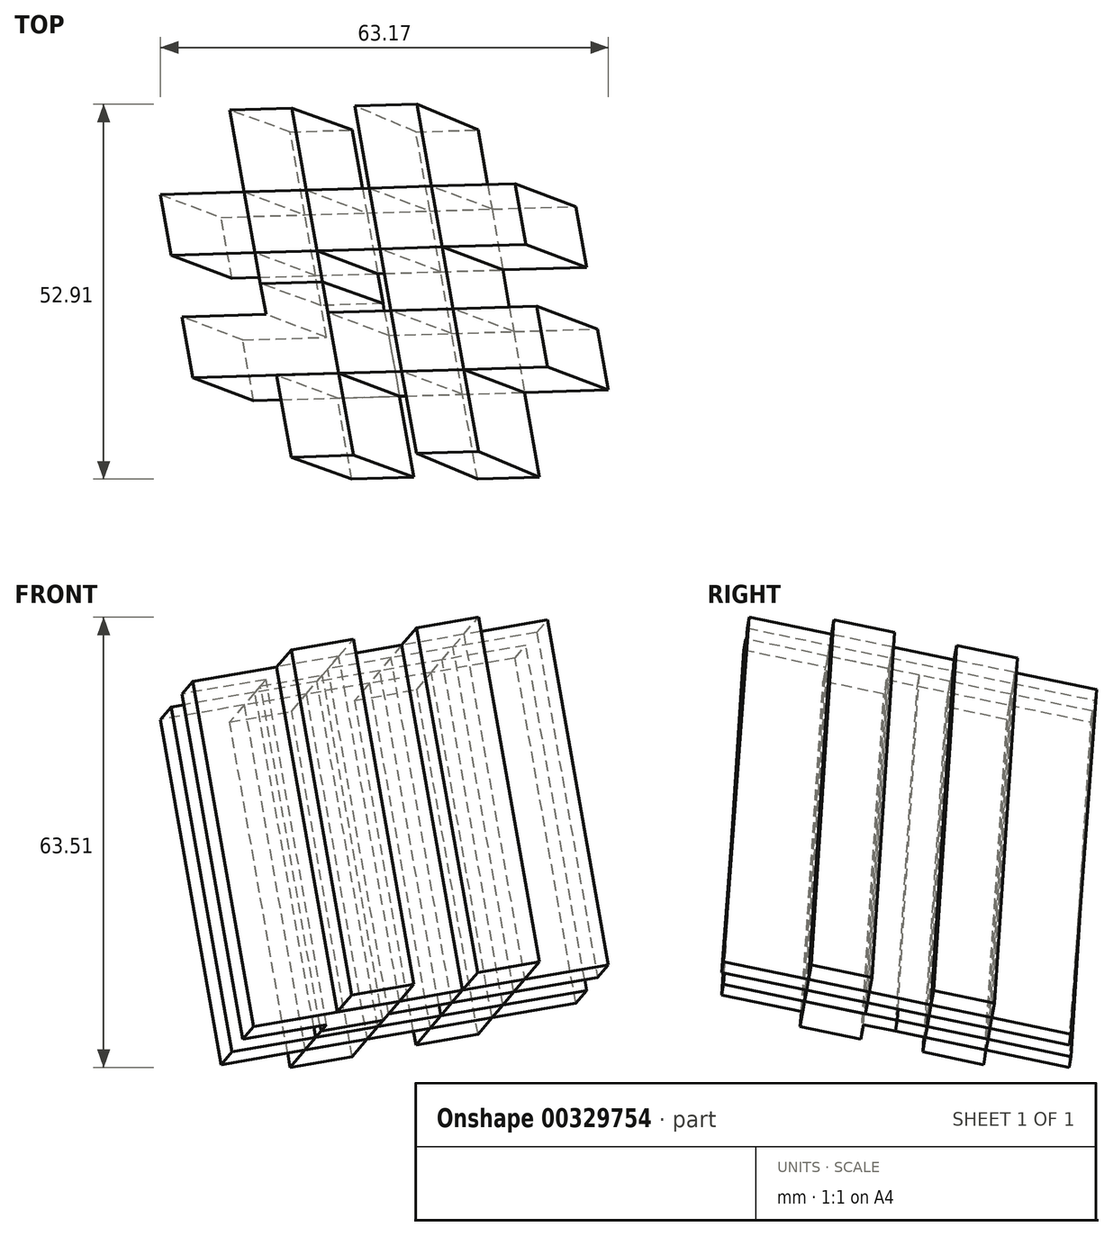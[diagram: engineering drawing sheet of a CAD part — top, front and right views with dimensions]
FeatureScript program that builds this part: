
annotation { "Feature Type Name" : "Feature", "Feature Type Description" : "" }
export const myFeature = defineFeature(function(context is Context, id is Id, definition is map)
    precondition{}
    {
        {
            var Q0;
            Q0=qCreatedBy(makeId("Front.planeOp"),FACE);
            var sketch = newSketch(context, id + "F0", { "sketchPlane" : qUnion([Q0])});
            skLineSegment(sketch, "E0", {"start": v(74.16, 50.8) * mm, "end": v(-71.4, 50.8) * mm});
            skSolve(sketch);
        }
        {
            var Q0;
            Q0=qCreatedBy(makeId("Top.planeOp"),FACE);
            var sketch = newSketch(context, id + "F1", { "sketchPlane" : qUnion([Q0])});
            skLineSegment(sketch, "E1", {"start": v(-74.62, 0) * mm, "end": v(72.22, 0) * mm});
            skSolve(sketch);
        }
        {
            var Q0;
            Q0=qCreatedBy(makeId("Top.planeOp"),FACE);
            var Q1;
            Q1=sQuery(id+"F1.wireOp",EDGE,"E1");
            cPlane(context, id + "F2", {"entities" : qUnion([Q0, Q1]), "cplaneType" : CPlaneType.LINE_ANGLE, "offset" : 0 * mm, "angle" : 170 * degree, "width" : 152.4 * mm, "height" : 152.4 * mm});
        }
        {
            var Q0;
            Q0=qCreatedBy(id+"F2.planeOp",FACE);
            var sketch = newSketch(context, id + "F3", { "sketchPlane" : qUnion([Q0])});
            skLineSegment(sketch, "E2", {"start": v(0, 68.21) * mm, "end": v(0, -63.3) * mm});
            skSolve(sketch);
        }
        {
            var Q0;
            Q0=sQuery(id+"F3.wireOp",EDGE,"E2");
            var Q1;
            Q1=qCreatedBy(id+"F2.planeOp",FACE);
            cPlane(context, id + "F4", {"entities" : qUnion([Q0, Q1]), "cplaneType" : CPlaneType.LINE_ANGLE, "offset" : 25.4 * mm, "angle" : 10 * degree, "width" : 152.4 * mm, "height" : 152.4 * mm});
        }
        {
            var Q0;
            Q0=qCreatedBy(id+"F4.planeOp",FACE);
            var sketch = newSketch(context, id + "F5", { "sketchPlane" : qUnion([Q0])});
            skLineSegment(sketch, "E3.bottom", {"start": v(-23.07, 13.2) * mm, "end": v(27.73, 13.2) * mm});
            skLineSegment(sketch, "E3.top", {"start": v(-24.62, 4.44) * mm, "end": v(26.18, 4.45) * mm});
            skLineSegment(sketch, "E3.left", {"start": v(-23.07, 13.2) * mm, "end": v(-24.62, 4.45) * mm});
            skLineSegment(sketch, "E3.right", {"start": v(27.73, 13.2) * mm, "end": v(26.18, 4.45) * mm});
            skLineSegment(sketch, "E4.bottom", {"start": v(-26.18, -4.45) * mm, "end": v(24.62, -4.44) * mm});
            skLineSegment(sketch, "E4.top", {"start": v(-27.73, -13.2) * mm, "end": v(23.07, -13.2) * mm});
            skLineSegment(sketch, "E4.left", {"start": v(-26.18, -4.45) * mm, "end": v(-27.73, -13.2) * mm});
            skLineSegment(sketch, "E4.right", {"start": v(24.62, -4.44) * mm, "end": v(23.07, -13.2) * mm});
            skLineSegment(sketch, "E5", {"start": v(-9.02, 24.88) * mm, "end": v(-17.84, -25.15) * mm});
            skLineSegment(sketch, "E6", {"start": v(-17.84, -25.15) * mm, "end": v(-8.95, -25.15) * mm});
            skLineSegment(sketch, "E7", {"start": v(-8.95, -25.15) * mm, "end": v(-0.13, 24.88) * mm});
            skLineSegment(sketch, "E8", {"start": v(-0.13, 24.88) * mm, "end": v(-9.02, 24.88) * mm});
            skLineSegment(sketch, "E9", {"start": v(0.78, 4.45) * mm, "end": v(-0.78, -4.45) * mm});
            skPoint(sketch, "E10", {"position": v(0, 0) * mm});
            skPoint(sketch, "E11", {"position": v(-4.54, -0.14) * mm});
            skLineSegment(sketch, "E12", {"start": v(9, 25.43) * mm, "end": v(0.18, -24.6) * mm});
            skLineSegment(sketch, "E13", {"start": v(0.18, -24.6) * mm, "end": v(9.07, -24.6) * mm});
            skLineSegment(sketch, "E14", {"start": v(9.07, -24.6) * mm, "end": v(17.89, 25.43) * mm});
            skLineSegment(sketch, "E15", {"start": v(17.89, 25.43) * mm, "end": v(9, 25.43) * mm});
            skPoint(sketch, "E16", {"position": v(13.48, 0.41) * mm});
            skPoint(sketch, "E17", {"position": v(4.54, 0.14) * mm});
            skLineSegment(sketch, "E18", {"start": v(4.54, 0.14) * mm, "end": v(0, 0) * mm});
            skLineSegment(sketch, "E19", {"start": v(-4.54, -0.14) * mm, "end": v(0, 0) * mm});
            skLineSegment(sketch, "E20", {"start": v(0.78, 4.45) * mm, "end": v(0, 0) * mm});
            skLineSegment(sketch, "E21", {"start": v(-4.54, -0.14) * mm, "end": v(-13.43, -0.14) * mm});
            skPoint(sketch, "E22", {"position": v(2.19, -13.2) * mm});
            skPoint(sketch, "E23", {"position": v(-14.19, -4.45) * mm});
            skSolve(sketch);
        }
        {
            var Q0;
            Q0=qCreatedBy(makeId("Top.planeOp"),FACE);
            var Q1;
            Q1=sQuery(id+"F0.wireOp",EDGE,"E0");
            cPlane(context, id + "F6", {"entities" : qUnion([Q0, Q1]), "cplaneType" : CPlaneType.LINE_ANGLE, "offset" : 50.8 * mm, "angle" : 10 * degree, "width" : 152.4 * mm, "height" : 152.4 * mm});
        }
        {
            var Q0;
            Q0=qCreatedBy(id+"F6.planeOp",FACE);
            var sketch = newSketch(context, id + "F7", { "sketchPlane" : qUnion([Q0])});
            skLineSegment(sketch, "E24", {"start": v(0, -55.77) * mm, "end": v(0, 79.16) * mm});
            skSolve(sketch);
        }
        {
            var Q0;
            Q0=sQuery(id+"F7.wireOp",EDGE,"E24");
            var Q1;
            Q1=qCreatedBy(id+"F6.planeOp",FACE);
            cPlane(context, id + "F8", {"entities" : qUnion([Q0, Q1]), "cplaneType" : CPlaneType.LINE_ANGLE, "offset" : 25.4 * mm, "angle" : 10 * degree, "width" : 152.4 * mm, "height" : 152.4 * mm});
        }
        {
            var Q0;
            Q0=qCreatedBy(id+"F8.planeOp",FACE);
            var sketch = newSketch(context, id + "F9", { "sketchPlane" : qUnion([Q0])});
            skLineSegment(sketch, "E25.bottom", {"start": v(-130.18, 7.92) * mm, "end": v(-79.38, 7.92) * mm});
            skLineSegment(sketch, "E25.top", {"start": v(-131.73, -0.83) * mm, "end": v(-80.93, -0.83) * mm});
            skLineSegment(sketch, "E25.left", {"start": v(-130.18, 7.92) * mm, "end": v(-131.73, -0.83) * mm});
            skLineSegment(sketch, "E25.right", {"start": v(-79.38, 7.92) * mm, "end": v(-80.93, -0.83) * mm});
            skLineSegment(sketch, "E26.bottom", {"start": v(-133.3, -9.72) * mm, "end": v(-82.5, -9.72) * mm});
            skLineSegment(sketch, "E26.top", {"start": v(-134.84, -18.48) * mm, "end": v(-84.04, -18.48) * mm});
            skLineSegment(sketch, "E26.left", {"start": v(-133.3, -9.72) * mm, "end": v(-134.84, -18.48) * mm});
            skLineSegment(sketch, "E26.right", {"start": v(-82.5, -9.72) * mm, "end": v(-84.04, -18.48) * mm});
            skLineSegment(sketch, "E27", {"start": v(-116.1, 19.74) * mm, "end": v(-124.92, -30.29) * mm});
            skLineSegment(sketch, "E28", {"start": v(-124.92, -30.29) * mm, "end": v(-116.03, -30.29) * mm});
            skLineSegment(sketch, "E29", {"start": v(-116.03, -30.29) * mm, "end": v(-107.21, 19.74) * mm});
            skLineSegment(sketch, "E30", {"start": v(-107.21, 19.74) * mm, "end": v(-116.1, 19.74) * mm});
            skLineSegment(sketch, "E31", {"start": v(-106.33, -0.83) * mm, "end": v(-107.9, -9.72) * mm});
            skPoint(sketch, "E32", {"position": v(-107.1, -5.28) * mm});
            skPoint(sketch, "E33", {"position": v(-111.62, -5.28) * mm});
            skLineSegment(sketch, "E34", {"start": v(-98.19, 19.74) * mm, "end": v(-107, -30.29) * mm});
            skLineSegment(sketch, "E35", {"start": v(-107, -30.29) * mm, "end": v(-98.12, -30.29) * mm});
            skLineSegment(sketch, "E36", {"start": v(-98.12, -30.29) * mm, "end": v(-89.3, 19.74) * mm});
            skLineSegment(sketch, "E37", {"start": v(-89.3, 19.74) * mm, "end": v(-98.19, 19.74) * mm});
            skLineSegment(sketch, "E38", {"start": v(-111.62, -5.28) * mm, "end": v(-107.1, -5.28) * mm});
            skLineSegment(sketch, "E39", {"start": v(-106.33, -0.83) * mm, "end": v(-107.1, -5.28) * mm});
            skPoint(sketch, "E40", {"position": v(-102.6, -5.28) * mm});
            skLineSegment(sketch, "E41", {"start": v(-107.1, -5.28) * mm, "end": v(-102.6, -5.28) * mm});
            skLineSegment(sketch, "E42.MirrorCS", {"start": v(124.48, -5.28) * mm, "end": v(119.97, -5.28) * mm});
            skLineSegment(sketch, "E43.MirrorCS", {"start": v(123.7, -0.83) * mm, "end": v(124.48, -5.28) * mm});
            skLineSegment(sketch, "E44.MirrorCS", {"start": v(129, -5.28) * mm, "end": v(124.48, -5.28) * mm});
            skLineSegment(sketch, "E45.MirrorCS", {"start": v(123.7, -0.83) * mm, "end": v(125.27, -9.72) * mm});
            skLineSegment(sketch, "E46.MirrorCS", {"start": v(115.5, -30.29) * mm, "end": v(106.67, 19.74) * mm});
            skLineSegment(sketch, "E47.MirrorCS", {"start": v(147.56, 7.92) * mm, "end": v(96.76, 7.92) * mm});
            skLineSegment(sketch, "E48.MirrorCS", {"start": v(152.21, -18.48) * mm, "end": v(101.41, -18.48) * mm});
            skPoint(sketch, "E49.MirrorP", {"position": v(124.48, -5.28) * mm});
            skPoint(sketch, "E50.MirrorP", {"position": v(129, -5.28) * mm});
            skPoint(sketch, "E51.MirrorP", {"position": v(119.97, -5.28) * mm});
            skLineSegment(sketch, "E52.MirrorCS", {"start": v(124.59, 19.74) * mm, "end": v(133.48, 19.74) * mm});
            skLineSegment(sketch, "E53.MirrorCS", {"start": v(150.67, -9.72) * mm, "end": v(152.21, -18.48) * mm});
            skLineSegment(sketch, "E54.MirrorCS", {"start": v(149.1, -0.83) * mm, "end": v(98.3, -0.83) * mm});
            skLineSegment(sketch, "E55.MirrorCS", {"start": v(142.3, -30.29) * mm, "end": v(133.4, -30.29) * mm});
            skLineSegment(sketch, "E56.MirrorCS", {"start": v(124.38, -30.29) * mm, "end": v(115.5, -30.29) * mm});
            skLineSegment(sketch, "E57.MirrorCS", {"start": v(133.48, 19.74) * mm, "end": v(142.3, -30.29) * mm});
            skLineSegment(sketch, "E58.MirrorCS", {"start": v(147.56, 7.92) * mm, "end": v(149.1, -0.83) * mm});
            skLineSegment(sketch, "E59.MirrorCS", {"start": v(115.56, 19.74) * mm, "end": v(124.38, -30.29) * mm});
            skLineSegment(sketch, "E60.MirrorCS", {"start": v(150.67, -9.72) * mm, "end": v(99.87, -9.72) * mm});
            skLineSegment(sketch, "E61.MirrorCS", {"start": v(96.76, 7.92) * mm, "end": v(98.3, -0.83) * mm});
            skLineSegment(sketch, "E62.MirrorCS", {"start": v(133.4, -30.29) * mm, "end": v(124.59, 19.74) * mm});
            skLineSegment(sketch, "E63.MirrorCS", {"start": v(99.87, -9.72) * mm, "end": v(101.41, -18.48) * mm});
            skLineSegment(sketch, "E64.MirrorCS", {"start": v(106.67, 19.74) * mm, "end": v(115.56, 19.74) * mm});
            skLineSegment(sketch, "E65", {"start": v(-107.1, -5.28) * mm, "end": v(0, -5.28) * mm});
            skPoint(sketch, "E66", {"position": v(-53.55, -5.28) * mm});
            skPoint(sketch, "E67", {"position": v(-53.55, -7.97) * mm});
            skLineSegment(sketch, "E68", {"start": v(-53.55, -7.97) * mm, "end": v(-53.55, -5.28) * mm});
            skLineSegment(sketch, "E69.MirrorCS", {"start": v(0, -5.28) * mm, "end": v(-4.51, -5.28) * mm});
            skLineSegment(sketch, "E70.MirrorCS", {"start": v(-0.78, -0.83) * mm, "end": v(0, -5.28) * mm});
            skLineSegment(sketch, "E71.MirrorCS", {"start": v(-0.1, -30.29) * mm, "end": v(-9, -30.29) * mm});
            skLineSegment(sketch, "E72.MirrorCS", {"start": v(0.1, 19.74) * mm, "end": v(9, 19.74) * mm});
            skLineSegment(sketch, "E73.MirrorCS", {"start": v(23.07, 7.92) * mm, "end": v(24.62, -0.83) * mm});
            skLineSegment(sketch, "E74.MirrorCS", {"start": v(17.81, -30.29) * mm, "end": v(8.92, -30.29) * mm});
            skLineSegment(sketch, "E75.MirrorCS", {"start": v(26.18, -9.72) * mm, "end": v(27.73, -18.48) * mm});
            skLineSegment(sketch, "E76.MirrorCS", {"start": v(-24.62, -9.72) * mm, "end": v(-23.07, -18.48) * mm});
            skLineSegment(sketch, "E77.MirrorCS", {"start": v(-27.73, 7.92) * mm, "end": v(-26.18, -0.83) * mm});
            skLineSegment(sketch, "E78.MirrorCS", {"start": v(4.51, -5.28) * mm, "end": v(0, -5.28) * mm});
            skLineSegment(sketch, "E79.MirrorCS", {"start": v(-17.81, 19.74) * mm, "end": v(-8.92, 19.74) * mm});
            skLineSegment(sketch, "E80.MirrorCS", {"start": v(-0.78, -0.83) * mm, "end": v(0.78, -9.72) * mm});
            skLineSegment(sketch, "E81.MirrorCS", {"start": v(-9, -30.29) * mm, "end": v(-17.81, 19.74) * mm});
            skLineSegment(sketch, "E82.MirrorCS", {"start": v(23.07, 7.92) * mm, "end": v(-27.73, 7.92) * mm});
            skLineSegment(sketch, "E83.MirrorCS", {"start": v(9, 19.74) * mm, "end": v(17.81, -30.29) * mm});
            skLineSegment(sketch, "E84.MirrorCS", {"start": v(26.18, -9.72) * mm, "end": v(-24.62, -9.72) * mm});
            skLineSegment(sketch, "E85.MirrorCS", {"start": v(27.73, -18.48) * mm, "end": v(-23.07, -18.48) * mm});
            skPoint(sketch, "E86.MirrorP", {"position": v(4.51, -5.28) * mm});
            skPoint(sketch, "E87.MirrorP", {"position": v(0, -5.28) * mm});
            skLineSegment(sketch, "E88.MirrorCS", {"start": v(8.92, -30.29) * mm, "end": v(0.1, 19.74) * mm});
            skPoint(sketch, "E89.MirrorP", {"position": v(-4.51, -5.28) * mm});
            skLineSegment(sketch, "E90.MirrorCS", {"start": v(-8.92, 19.74) * mm, "end": v(-0.1, -30.29) * mm});
            skLineSegment(sketch, "E91.MirrorCS", {"start": v(24.62, -0.83) * mm, "end": v(-26.18, -0.83) * mm});
            skSolve(sketch);
        }
        {
            var Q0;
            {var subQ0=sQuery(id+"F9.wireOp",EDGE,"E83.MirrorCS");var subQ1=sQuery(id+"F9.wireOp",EDGE,"E82.MirrorCS");var subQ2=makeQuery(id+"F9.imprint","INTERSECT",VERTEX,{"derivedFrom":[subQ1,subQ0]});Q0=makeQuery(id+"F9.imprint","IMPRINT",FACE,{"disambiguationData":[TD([[makeQuery(id+"F9.imprint","IMPRINT",EDGE,{"disambiguationData":[TD([[subQ2,-1.0]])],"derivedFrom":subQ1}),1.0]])]});}
            var Q1;
            {var subQ0=sQuery(id+"F5.wireOp",EDGE,"E14");var subQ1=sQuery(id+"F5.wireOp",EDGE,"E4.bottom");var subQ2=makeQuery(id+"F5.imprint","INTERSECT",VERTEX,{"derivedFrom":[subQ1,subQ0]});Q1=makeQuery(id+"F5.imprint","IMPRINT",FACE,{"disambiguationData":[TD([[makeQuery(id+"F5.imprint","IMPRINT",EDGE,{"disambiguationData":[TD([[subQ2,1.0]])],"derivedFrom":subQ1}),-1.0]])]});}
            loft(context, id + "F10", {"sheetProfilesArray" : [{ "sheetProfileEntities" : qUnion([Q0]) }, { "sheetProfileEntities" : qUnion([Q1]) }]});
        }
        {
            var Q0;
            {var subQ0=sQuery(id+"F5.wireOp",EDGE,"E5");var subQ1=sQuery(id+"F5.wireOp",EDGE,"E4.bottom");var subQ2=makeQuery(id+"F5.imprint","INTERSECT",VERTEX,{"derivedFrom":[subQ1,subQ0]});Q0=makeQuery(id+"F5.imprint","IMPRINT",FACE,{"disambiguationData":[TD([[makeQuery(id+"F5.imprint","IMPRINT",EDGE,{"disambiguationData":[TD([[subQ2,-1.0]])],"derivedFrom":subQ1}),-1.0]])]});}
            var Q1;
            {var subQ0=sQuery(id+"F9.wireOp",EDGE,"E91.MirrorCS");var subQ1=sQuery(id+"F9.wireOp",EDGE,"E81.MirrorCS");var subQ2=makeQuery(id+"F9.imprint","INTERSECT",VERTEX,{"derivedFrom":[subQ1,subQ0]});Q1=makeQuery(id+"F9.imprint","IMPRINT",FACE,{"disambiguationData":[TD([[makeQuery(id+"F9.imprint","IMPRINT",EDGE,{"disambiguationData":[TD([[subQ2,-1.0]])],"derivedFrom":subQ1}),-1.0]])]});}
            loft(context, id + "F11", {"sheetProfilesArray" : [{ "sheetProfileEntities" : qUnion([Q0]) }, { "sheetProfileEntities" : qUnion([Q1]) }]});
        }
        {
            var Q0;
            {var subQ0=sQuery(id+"F9.wireOp",EDGE,"E85.MirrorCS");var subQ1=sQuery(id+"F9.wireOp",EDGE,"E81.MirrorCS");var subQ2=makeQuery(id+"F9.imprint","INTERSECT",VERTEX,{"derivedFrom":[subQ1,subQ0]});Q0=makeQuery(id+"F9.imprint","IMPRINT",FACE,{"disambiguationData":[TD([[makeQuery(id+"F9.imprint","IMPRINT",EDGE,{"disambiguationData":[TD([[subQ2,-1.0]])],"derivedFrom":subQ1}),-1.0]])]});}
            var Q1;
            {var subQ0=sQuery(id+"F5.wireOp",EDGE,"E5");var subQ1=sQuery(id+"F5.wireOp",EDGE,"E3.bottom");var subQ2=makeQuery(id+"F5.imprint","INTERSECT",VERTEX,{"derivedFrom":[subQ1,subQ0]});Q1=makeQuery(id+"F5.imprint","IMPRINT",FACE,{"disambiguationData":[TD([[makeQuery(id+"F5.imprint","IMPRINT",EDGE,{"disambiguationData":[TD([[subQ2,-1.0]])],"derivedFrom":subQ1}),-1.0]])]});}
            loft(context, id + "F12", {"sheetProfilesArray" : [{ "sheetProfileEntities" : qUnion([Q0]) }, { "sheetProfileEntities" : qUnion([Q1]) }]});
        }
        {
            var Q0;
            {var subQ0=sQuery(id+"F9.wireOp",EDGE,"E84.MirrorCS");var subQ1=sQuery(id+"F9.wireOp",EDGE,"E83.MirrorCS");var subQ2=makeQuery(id+"F9.imprint","INTERSECT",VERTEX,{"derivedFrom":[subQ1,subQ0]});Q0=makeQuery(id+"F9.imprint","IMPRINT",FACE,{"disambiguationData":[TD([[makeQuery(id+"F9.imprint","IMPRINT",EDGE,{"disambiguationData":[TD([[subQ2,-1.0]])],"derivedFrom":subQ1}),-1.0]])]});}
            var Q1;
            {var subQ0=sQuery(id+"F5.wireOp",EDGE,"E12");var subQ1=sQuery(id+"F5.wireOp",EDGE,"E3.bottom");var subQ2=makeQuery(id+"F5.imprint","INTERSECT",VERTEX,{"derivedFrom":[subQ1,subQ0]});Q1=makeQuery(id+"F5.imprint","IMPRINT",FACE,{"disambiguationData":[TD([[makeQuery(id+"F5.imprint","IMPRINT",EDGE,{"disambiguationData":[TD([[subQ2,-1.0]])],"derivedFrom":subQ1}),-1.0]])]});}
            loft(context, id + "F13", {"sheetProfilesArray" : [{ "sheetProfileEntities" : qUnion([Q0]) }, { "sheetProfileEntities" : qUnion([Q1]) }]});
        }
        {
            var Q0;
            {var subQ0=sQuery(id+"F5.wireOp",EDGE,"E3.left");Q0=makeQuery(id+"F5.imprint","IMPRINT",FACE,{"disambiguationData":[TD([[makeQuery(id+"F5.imprint","IMPRINT",EDGE,{"derivedFrom":subQ0}),1.0]])]});}
            var Q1;
            {var subQ0=sQuery(id+"F9.wireOp",EDGE,"E76.MirrorCS");Q1=makeQuery(id+"F9.imprint","IMPRINT",FACE,{"disambiguationData":[TD([[makeQuery(id+"F9.imprint","IMPRINT",EDGE,{"derivedFrom":subQ0}),1.0]])]});}
            loft(context, id + "F14", {"sheetProfilesArray" : [{ "sheetProfileEntities" : qUnion([Q0]) }, { "sheetProfileEntities" : qUnion([Q1]) }]});
        }
        {
            var Q0;
            {var subQ0=sQuery(id+"F9.wireOp",EDGE,"E77.MirrorCS");Q0=makeQuery(id+"F9.imprint","IMPRINT",FACE,{"disambiguationData":[TD([[makeQuery(id+"F9.imprint","IMPRINT",EDGE,{"derivedFrom":subQ0}),1.0]])]});}
            var Q1;
            {var subQ0=sQuery(id+"F5.wireOp",EDGE,"E4.left");Q1=makeQuery(id+"F5.imprint","IMPRINT",FACE,{"disambiguationData":[TD([[makeQuery(id+"F5.imprint","IMPRINT",EDGE,{"derivedFrom":subQ0}),1.0]])]});}
            loft(context, id + "F15", {"sheetProfilesArray" : [{ "sheetProfileEntities" : qUnion([Q0]) }, { "sheetProfileEntities" : qUnion([Q1]) }]});
        }
        {
            var Q0;
            {var subQ5=sQuery(id+"F5.wireOp",EDGE,"E6");Q0=makeQuery(id+"F5.imprint","IMPRINT",FACE,{"disambiguationData":[TD([[makeQuery(id+"F5.imprint","IMPRINT",EDGE,{"derivedFrom":subQ5}),1.0]])]});}
            var Q1;
            {var subQ0=sQuery(id+"F9.wireOp",EDGE,"E79.MirrorCS");Q1=makeQuery(id+"F9.imprint","IMPRINT",FACE,{"disambiguationData":[TD([[makeQuery(id+"F9.imprint","IMPRINT",EDGE,{"derivedFrom":subQ0}),-1.0]])]});}
            loft(context, id + "F16", {"sheetProfilesArray" : [{ "sheetProfileEntities" : qUnion([Q0]) }, { "sheetProfileEntities" : qUnion([Q1]) }]});
        }
        {
            var Q0;
            {var subQ5=sQuery(id+"F5.wireOp",EDGE,"E13");Q0=makeQuery(id+"F5.imprint","IMPRINT",FACE,{"disambiguationData":[TD([[makeQuery(id+"F5.imprint","IMPRINT",EDGE,{"derivedFrom":subQ5}),1.0]])]});}
            var Q1;
            {var subQ0=sQuery(id+"F9.wireOp",EDGE,"E72.MirrorCS");Q1=makeQuery(id+"F9.imprint","IMPRINT",FACE,{"disambiguationData":[TD([[makeQuery(id+"F9.imprint","IMPRINT",EDGE,{"derivedFrom":subQ0}),-1.0]])]});}
            loft(context, id + "F17", {"sheetProfilesArray" : [{ "sheetProfileEntities" : qUnion([Q0]) }, { "sheetProfileEntities" : qUnion([Q1]) }]});
        }
        {
            var Q0;
            {var subQ0=sQuery(id+"F5.wireOp",EDGE,"E4.right");Q0=makeQuery(id+"F5.imprint","IMPRINT",FACE,{"disambiguationData":[TD([[makeQuery(id+"F5.imprint","IMPRINT",EDGE,{"derivedFrom":subQ0}),-1.0]])]});}
            var Q1;
            {var subQ0=sQuery(id+"F9.wireOp",EDGE,"E73.MirrorCS");Q1=makeQuery(id+"F9.imprint","IMPRINT",FACE,{"disambiguationData":[TD([[makeQuery(id+"F9.imprint","IMPRINT",EDGE,{"derivedFrom":subQ0}),-1.0]])]});}
            loft(context, id + "F18", {"sheetProfilesArray" : [{ "sheetProfileEntities" : qUnion([Q0]) }, { "sheetProfileEntities" : qUnion([Q1]) }]});
        }
        {
            var Q0;
            {var subQ0=sQuery(id+"F9.wireOp",EDGE,"E75.MirrorCS");Q0=makeQuery(id+"F9.imprint","IMPRINT",FACE,{"disambiguationData":[TD([[makeQuery(id+"F9.imprint","IMPRINT",EDGE,{"derivedFrom":subQ0}),-1.0]])]});}
            var Q1;
            {var subQ0=sQuery(id+"F5.wireOp",EDGE,"E3.right");Q1=makeQuery(id+"F5.imprint","IMPRINT",FACE,{"disambiguationData":[TD([[makeQuery(id+"F5.imprint","IMPRINT",EDGE,{"derivedFrom":subQ0}),-1.0]])]});}
            loft(context, id + "F19", {"sheetProfilesArray" : [{ "sheetProfileEntities" : qUnion([Q0]) }, { "sheetProfileEntities" : qUnion([Q1]) }]});
        }
        {
            var Q0;
            {var subQ5=sQuery(id+"F5.wireOp",EDGE,"E15");Q0=makeQuery(id+"F5.imprint","IMPRINT",FACE,{"disambiguationData":[TD([[makeQuery(id+"F5.imprint","IMPRINT",EDGE,{"derivedFrom":subQ5}),1.0]])]});}
            var Q1;
            {var subQ0=sQuery(id+"F9.wireOp",EDGE,"E74.MirrorCS");Q1=makeQuery(id+"F9.imprint","IMPRINT",FACE,{"disambiguationData":[TD([[makeQuery(id+"F9.imprint","IMPRINT",EDGE,{"derivedFrom":subQ0}),-1.0]])]});}
            loft(context, id + "F20", {"sheetProfilesArray" : [{ "sheetProfileEntities" : qUnion([Q0]) }, { "sheetProfileEntities" : qUnion([Q1]) }]});
        }
        {
            var Q0;
            {var subQ5=sQuery(id+"F5.wireOp",EDGE,"E8");Q0=makeQuery(id+"F5.imprint","IMPRINT",FACE,{"disambiguationData":[TD([[makeQuery(id+"F5.imprint","IMPRINT",EDGE,{"derivedFrom":subQ5}),1.0]])]});}
            var Q1;
            {var subQ0=sQuery(id+"F9.wireOp",EDGE,"E71.MirrorCS");Q1=makeQuery(id+"F9.imprint","IMPRINT",FACE,{"disambiguationData":[TD([[makeQuery(id+"F9.imprint","IMPRINT",EDGE,{"derivedFrom":subQ0}),-1.0]])]});}
            loft(context, id + "F21", {"sheetProfilesArray" : [{ "sheetProfileEntities" : qUnion([Q0]) }, { "sheetProfileEntities" : qUnion([Q1]) }]});
        }
        {
            var Q0;
            {var subQ1=sQuery(id+"F9.wireOp",EDGE,"E82.MirrorCS");var subQ6=sQuery(id+"F9.wireOp",EDGE,"E88.MirrorCS");var subQ8=makeQuery(id+"F9.imprint","INTERSECT",VERTEX,{"derivedFrom":[subQ1,subQ6]});Q0=makeQuery(id+"F9.imprint","IMPRINT",FACE,{"disambiguationData":[TD([[makeQuery(id+"F9.imprint","IMPRINT",EDGE,{"disambiguationData":[TD([[subQ8,-1.0]])],"derivedFrom":subQ1}),1.0]])]});}
            var Q1;
            {var subQ3=sQuery(id+"F5.wireOp",EDGE,"E4.bottom");var subQ8=makeQuery(id+"F5.imprint","INTERSECT",VERTEX,{"derivedFrom":[subQ3,sQuery(id+"F5.wireOp",EDGE,"E9")]});Q1=makeQuery(id+"F5.imprint","IMPRINT",FACE,{"disambiguationData":[TD([[makeQuery(id+"F5.imprint","IMPRINT",EDGE,{"disambiguationData":[TD([[subQ8,1.0]])],"derivedFrom":subQ3}),-1.0]])]});}
            loft(context, id + "F22", {"sheetProfilesArray" : [{ "sheetProfileEntities" : qUnion([Q0]) }, { "sheetProfileEntities" : qUnion([Q1]) }]});
        }
        {
            var Q0;
            {var subQ4=sQuery(id+"F5.wireOp",EDGE,"E3.top");var subQ6=sQuery(id+"F5.wireOp",EDGE,"E14");var subQ7=makeQuery(id+"F5.imprint","INTERSECT",VERTEX,{"derivedFrom":[subQ4,subQ6]});Q0=makeQuery(id+"F5.imprint","IMPRINT",FACE,{"disambiguationData":[TD([[makeQuery(id+"F5.imprint","IMPRINT",EDGE,{"disambiguationData":[TD([[subQ7,1.0]])],"derivedFrom":subQ4}),-1.0]])]});}
            var Q1;
            {var subQ2=sQuery(id+"F9.wireOp",EDGE,"E91.MirrorCS");var subQ6=sQuery(id+"F9.wireOp",EDGE,"E83.MirrorCS");var subQ7=makeQuery(id+"F9.imprint","INTERSECT",VERTEX,{"derivedFrom":[subQ6,subQ2]});Q1=makeQuery(id+"F9.imprint","IMPRINT",FACE,{"disambiguationData":[TD([[makeQuery(id+"F9.imprint","IMPRINT",EDGE,{"disambiguationData":[TD([[subQ7,-1.0]])],"derivedFrom":subQ6}),-1.0]])]});}
            loft(context, id + "F23", {"sheetProfilesArray" : [{ "sheetProfileEntities" : qUnion([Q0]) }, { "sheetProfileEntities" : qUnion([Q1]) }]});
        }
        {
            var Q1;
            {var subQ5=sQuery(id+"F5.wireOp",EDGE,"E21");Q1=makeQuery(id+"F5.imprint","IMPRINT",FACE,{"disambiguationData":[TD([[makeQuery(id+"F5.imprint","IMPRINT",EDGE,{"derivedFrom":subQ5}),-1.0]])]});}
            var Q2;
            {var subQ1=sQuery(id+"F9.wireOp",EDGE,"E65");var subQ3=sQuery(id+"F9.wireOp",EDGE,"E81.MirrorCS");var subQ4=makeQuery(id+"F9.imprint","INTERSECT",VERTEX,{"derivedFrom":[subQ1,subQ3]});Q2=makeQuery(id+"F9.imprint","IMPRINT",FACE,{"disambiguationData":[TD([[makeQuery(id+"F9.imprint","IMPRINT",EDGE,{"disambiguationData":[TD([[subQ4,1.0]])],"derivedFrom":subQ3}),-1.0]])]});}
            loft(context, id + "F24", {"operationType" : NewBodyOperationType.ADD, "sheetProfilesArray" : [{ "sheetProfileEntities" : qUnion([Q1]) }, { "sheetProfileEntities" : qUnion([Q2]) }]});
        }
        {
            var Q0;
            {var subQ5=sQuery(id+"F5.wireOp",EDGE,"E21");Q0=makeQuery(id+"F5.imprint","IMPRINT",FACE,{"disambiguationData":[TD([[makeQuery(id+"F5.imprint","IMPRINT",EDGE,{"derivedFrom":subQ5}),1.0]])]});}
            var Q1;
            {var subQ1=sQuery(id+"F9.wireOp",EDGE,"E65");var subQ3=sQuery(id+"F9.wireOp",EDGE,"E81.MirrorCS");var subQ4=makeQuery(id+"F9.imprint","INTERSECT",VERTEX,{"derivedFrom":[subQ1,subQ3]});Q1=makeQuery(id+"F9.imprint","IMPRINT",FACE,{"disambiguationData":[TD([[makeQuery(id+"F9.imprint","IMPRINT",EDGE,{"disambiguationData":[TD([[subQ4,-1.0]])],"derivedFrom":subQ3}),-1.0]])]});}
            loft(context, id + "F25", {"sheetProfilesArray" : [{ "sheetProfileEntities" : qUnion([Q0]) }, { "sheetProfileEntities" : qUnion([Q1]) }]});
        }
        {
            var Q0;
            {var subQ4=sQuery(id+"F5.wireOp",EDGE,"E7");var subQ5=sQuery(id+"F5.wireOp",EDGE,"E3.bottom");var subQ6=makeQuery(id+"F5.imprint","INTERSECT",VERTEX,{"derivedFrom":[subQ5,subQ4]});Q0=makeQuery(id+"F5.imprint","IMPRINT",FACE,{"disambiguationData":[TD([[makeQuery(id+"F5.imprint","IMPRINT",EDGE,{"disambiguationData":[TD([[subQ6,-1.0]])],"derivedFrom":subQ5}),-1.0]])]});}
            var Q1;
            {var subQ5=sQuery(id+"F9.wireOp",EDGE,"E84.MirrorCS");var subQ6=makeQuery(id+"F9.imprint","INTERSECT",VERTEX,{"derivedFrom":[sQuery(id+"F9.wireOp",EDGE,"E80.MirrorCS"),subQ5]});Q1=makeQuery(id+"F9.imprint","IMPRINT",FACE,{"disambiguationData":[TD([[makeQuery(id+"F9.imprint","IMPRINT",EDGE,{"disambiguationData":[TD([[subQ6,1.0]])],"derivedFrom":subQ5}),1.0]])]});}
            loft(context, id + "F26", {"sheetProfilesArray" : [{ "sheetProfileEntities" : qUnion([Q0]) }, { "sheetProfileEntities" : qUnion([Q1]) }]});
        }
    });
